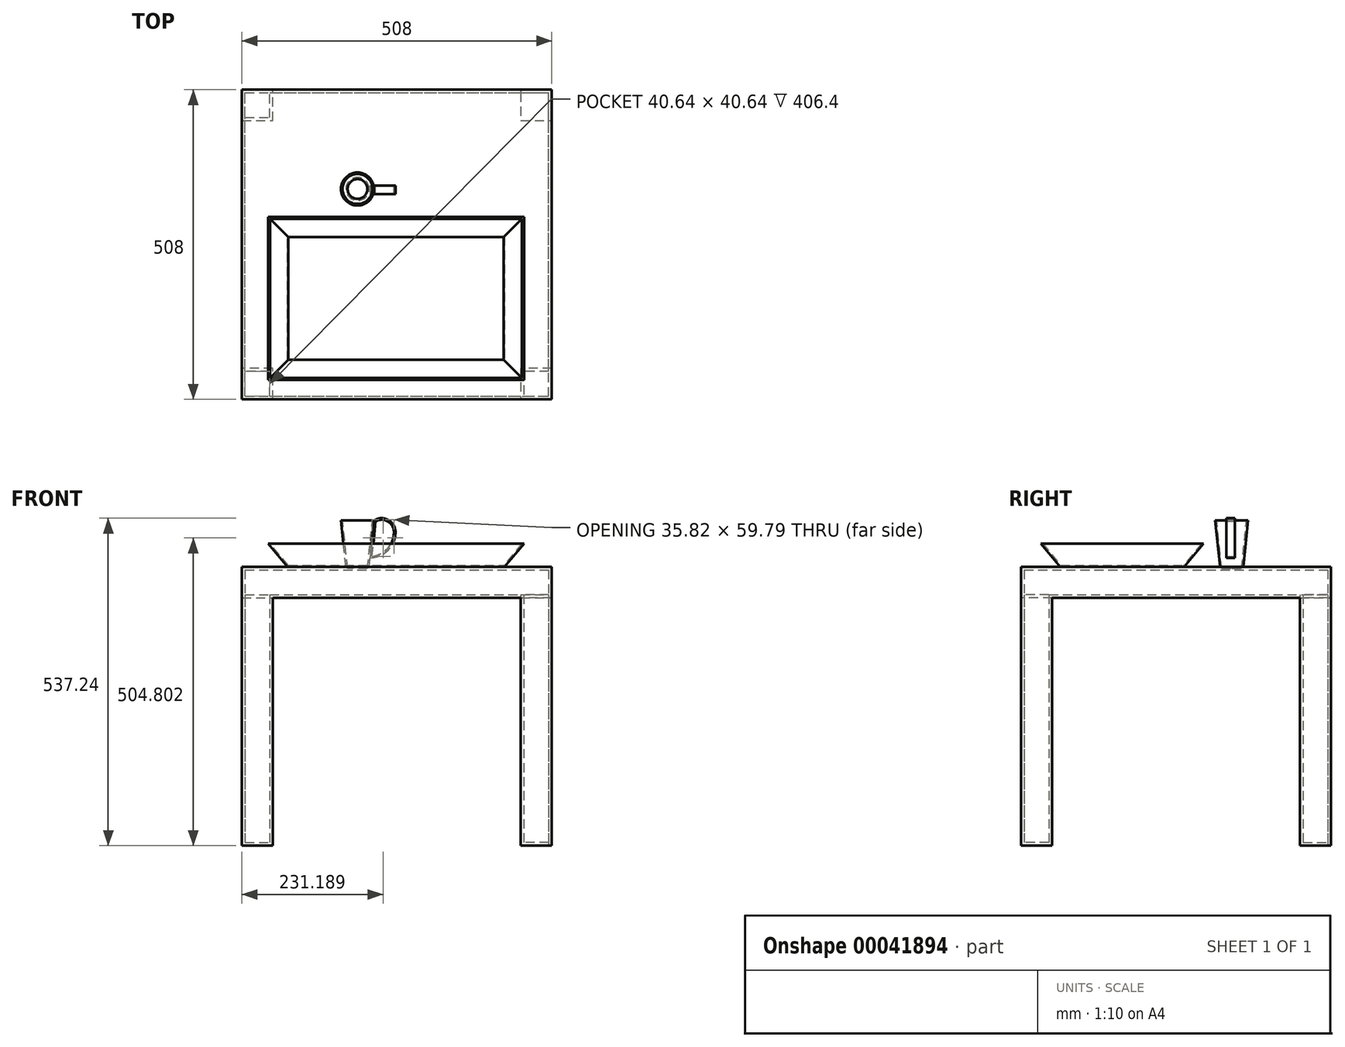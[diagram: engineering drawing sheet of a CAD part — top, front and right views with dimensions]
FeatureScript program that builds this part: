
annotation { "Feature Type Name" : "Feature", "Feature Type Description" : "" }
export const myFeature = defineFeature(function(context is Context, id is Id, definition is map)
    precondition{}
    {
        {
            var Q0;
            Q0=qCreatedBy(makeId("Front.planeOp"),FACE);
            var sketch = newSketch(context, id + "F0", { "sketchPlane" : qUnion([Q0])});
            skLineSegment(sketch, "E0.bottom", {"start": v(-251.64, 274.02) * mm, "end": v(256.36, 274.02) * mm});
            skLineSegment(sketch, "E0.top", {"start": v(-251.64, -183.18) * mm, "end": v(256.36, -183.18) * mm});
            skLineSegment(sketch, "E0.left", {"start": v(-251.64, 274.02) * mm, "end": v(-251.64, -183.18) * mm});
            skLineSegment(sketch, "E0.right", {"start": v(256.36, 274.02) * mm, "end": v(256.36, -183.18) * mm});
            skSolve(sketch);
        }
        {
            var Q0;
            Q0=makeQuery(id+"F0.imprint","IMPRINT",FACE,{"disambiguationData":[TD([[makeQuery(id+"F0.imprint","IMPRINT",EDGE,{"derivedFrom":sQuery(id+"F0.wireOp",EDGE,"E0.bottom")}),-1.0]])]});
            extrude(context, id + "F1", {"entities" : qUnion([Q0]), "depth" : 508 * mm});
        }
        {
            var Q0;
            Q0=makeQuery(id+"F1.opExtrude","SWEPT_FACE",FACE,{"disambiguationData":[OSD([sQuery(id+"F0.wireOp",EDGE,"E0.top")])]});
            var sketch = newSketch(context, id + "F2", { "sketchPlane" : qUnion([Q0])});
            skLineSegment(sketch, "E1", {"start": v(-251.64, 457.2) * mm, "end": v(-251.64, 50.8) * mm});
            skLineSegment(sketch, "E2", {"start": v(-251.64, 50.8) * mm, "end": v(-200.84, 50.8) * mm});
            skLineSegment(sketch, "E3", {"start": v(-200.84, 50.8) * mm, "end": v(-200.84, 0) * mm});
            skLineSegment(sketch, "E4", {"start": v(-200.84, 0) * mm, "end": v(205.56, 0) * mm});
            skLineSegment(sketch, "E5", {"start": v(205.56, 0) * mm, "end": v(205.56, 50.8) * mm});
            skLineSegment(sketch, "E6", {"start": v(205.56, 50.8) * mm, "end": v(256.36, 50.8) * mm});
            skLineSegment(sketch, "E7", {"start": v(256.36, 50.8) * mm, "end": v(256.36, 457.2) * mm});
            skLineSegment(sketch, "E8", {"start": v(256.36, 457.2) * mm, "end": v(205.56, 457.2) * mm});
            skLineSegment(sketch, "E9", {"start": v(205.56, 457.2) * mm, "end": v(205.56, 508) * mm});
            skLineSegment(sketch, "E10", {"start": v(205.56, 508) * mm, "end": v(-200.84, 508) * mm});
            skLineSegment(sketch, "E11", {"start": v(-200.84, 508) * mm, "end": v(-200.84, 457.2) * mm});
            skLineSegment(sketch, "E12", {"start": v(-200.84, 457.2) * mm, "end": v(-251.64, 457.2) * mm});
            skSolve(sketch);
        }
        {
            var Q0;
            Q0=makeQuery(id+"F2.imprint","IMPRINT",FACE,{"disambiguationData":[TD([[makeQuery(id+"F2.imprint","IMPRINT",EDGE,{"derivedFrom":sQuery(id+"F2.wireOp",EDGE,"E1")}),1.0]])]});
            extrude(context, id + "F3", {"entities" : qUnion([Q0]), "operationType" : NewBodyOperationType.REMOVE, "oppositeDirection" : true, "depth" : 406.4 * mm});
        }
        {
            var Q0;
            Q0=makeQuery(id+"F3.boolean.opBoolean","COPY",FACE,{"derivedFrom":makeQuery(id+"F3.opExtrude","SWEPT_FACE",FACE,{"disambiguationData":[OSD([sQuery(id+"F2.wireOp",EDGE,"E5")])]})});
            var Q1;
            Q1=makeQuery(id+"F3.boolean.opBoolean","COPY",FACE,{"derivedFrom":makeQuery(id+"F3.opExtrude","SWEPT_FACE",FACE,{"disambiguationData":[OSD([sQuery(id+"F2.wireOp",EDGE,"E6")])]})});
            var Q2;
            {var subQ0=sQuery(id+"F0.wireOp",EDGE,"E0.top");Q2=makeQuery(id+"F3.boolean.opBoolean","SPLIT",FACE,{"disambiguationData":[TD([makeQuery(id+"F3.opExtrude","SWEPT_FACE",FACE,{"disambiguationData":[OSD([sQuery(id+"F2.wireOp",EDGE,"E5")])]})])],"derivedFrom":makeQuery(id+"F1.opExtrude","SWEPT_FACE",FACE,{"disambiguationData":[OSD([subQ0])]})});}
            shell(context, id + "F4", {"entities" : qUnion([Q0, Q1, Q2]), "thickness" : 5.08 * mm});
        }
        {
            var Q0;
            Q0=makeQuery(id+"F1.opExtrude","SWEPT_FACE",FACE,{"disambiguationData":[OSD([sQuery(id+"F0.wireOp",EDGE,"E0.bottom")])]});
            var sketch = newSketch(context, id + "F5", { "sketchPlane" : qUnion([Q0])});
            skCircle(sketch, "E13", {"center": v(-62.25, -162.96) * mm, "radius": 19.05 * mm});
            skSolve(sketch);
        }
        {
            var Q0;
            Q0=makeQuery(id+"F5.imprint","IMPRINT",FACE,{"disambiguationData":[TD([[makeQuery(id+"F5.imprint","IMPRINT",EDGE,{"derivedFrom":sQuery(id+"F5.wireOp",EDGE,"E13")}),1.0]])]});
            extrude(context, id + "F6", {"entities" : qUnion([Q0]), "operationType" : NewBodyOperationType.ADD, "depth" : 76.2 * mm, "hasDraft" : true, "draftAngle" : 6 * degree});
        }
        {
            var Q0;
            Q0=makeQuery(id+"F6.opExtrude","CAP_FACE",FACE,{"disambiguationData":[OSD([sQuery(id+"F5.wireOp",EDGE,"E13")])],"isStart":false});
            shell(context, id + "F7", {"entities" : qUnion([Q0]), "thickness" : 2.54 * mm});
        }
        {
            var Q0;
            Q0=qCreatedBy(makeId("Front.planeOp"),FACE);
            var sketch = newSketch(context, id + "F8", { "sketchPlane" : qUnion([Q0])});
            skLineSegment(sketch, "E14", {"start": v(-41.18, 289) * mm, "end": v(-35.1, 350.45) * mm});
            skArc(sketch, "E15", {"start": v(0, 331.26) * mm, "mid": v(-11.86, 351.26) * mm, "end": v(-35.1, 350.45) * mm});
            skArc(sketch, "E16", {"start": v(0, 331.26) * mm, "mid": v(-12, 301.76) * mm, "end": v(-41.18, 289) * mm});
            skSolve(sketch);
        }
        {
            var Q0;
            Q0 = qSketchRegion(id + "F8", true);
            extrude(context, id + "F9", {"entities" : qUnion([Q0]), "depth" : 171.57 * mm});
        }
        {
            var Q0;
            Q0=makeQuery(id+"F8.imprint","IMPRINT",FACE,{"disambiguationData":[TD([[makeQuery(id+"F8.imprint","IMPRINT",EDGE,{"derivedFrom":sQuery(id+"F8.wireOp",EDGE,"E14")}),-1.0]])]});
            extrude(context, id + "F10", {"entities" : qUnion([Q0]), "operationType" : NewBodyOperationType.REMOVE, "depth" : 157.48 * mm});
        }
        {
            var Q0;
            Q0=makeQuery(id+"F10.boolean.opBoolean","COPY",FACE,{"derivedFrom":makeQuery(id+"F10.opExtrude","CAP_FACE",FACE,{"disambiguationData":[OSD([sQuery(id+"F8.wireOp",EDGE,"E14"),sQuery(id+"F8.wireOp",EDGE,"E15"),sQuery(id+"F8.wireOp",EDGE,"E16")])],"isStart":false})});
            var Q1;
            Q1=makeQuery(id+"F9.opExtrude","CAP_FACE",FACE,{"disambiguationData":[OSD([sQuery(id+"F8.wireOp",EDGE,"E14"),sQuery(id+"F8.wireOp",EDGE,"E15"),sQuery(id+"F8.wireOp",EDGE,"E16")])],"isStart":false});
            shell(context, id + "F11", {"entities" : qUnion([Q0, Q1]), "thickness" : 2.54 * mm});
        }
        {
            var Q0;
            Q0=makeQuery(id+"F1.opExtrude","SWEPT_FACE",FACE,{"disambiguationData":[OSD([sQuery(id+"F0.wireOp",EDGE,"E0.bottom")])]});
            var sketch = newSketch(context, id + "F12", { "sketchPlane" : qUnion([Q0])});
            skLineSegment(sketch, "E17.bottom", {"start": v(-176.92, -240.76) * mm, "end": v(178.68, -240.76) * mm});
            skLineSegment(sketch, "E17.top", {"start": v(-176.92, -443.96) * mm, "end": v(178.68, -443.96) * mm});
            skLineSegment(sketch, "E17.left", {"start": v(-176.92, -240.76) * mm, "end": v(-176.92, -443.96) * mm});
            skLineSegment(sketch, "E17.right", {"start": v(178.68, -240.76) * mm, "end": v(178.68, -443.96) * mm});
            skSolve(sketch);
        }
        {
            var Q0;
            Q0=makeQuery(id+"F12.imprint","IMPRINT",FACE,{"disambiguationData":[TD([[makeQuery(id+"F12.imprint","IMPRINT",EDGE,{"derivedFrom":sQuery(id+"F12.wireOp",EDGE,"E17.bottom")}),-1.0]])]});
            extrude(context, id + "F13", {"entities" : qUnion([Q0]), "depth" : 38.1 * mm, "hasDraft" : true, "draftAngle" : 40 * degree});
        }
        {
            var Q0;
            Q0=makeQuery(id+"F13.opExtrude","CAP_FACE",FACE,{"disambiguationData":[OSD([sQuery(id+"F12.wireOp",EDGE,"E17.bottom"),sQuery(id+"F12.wireOp",EDGE,"E17.top"),sQuery(id+"F12.wireOp",EDGE,"E17.left"),sQuery(id+"F12.wireOp",EDGE,"E17.right")])],"isStart":false});
            shell(context, id + "F14", {"entities" : qUnion([Q0]), "thickness" : 2.54 * mm});
        }
    });
